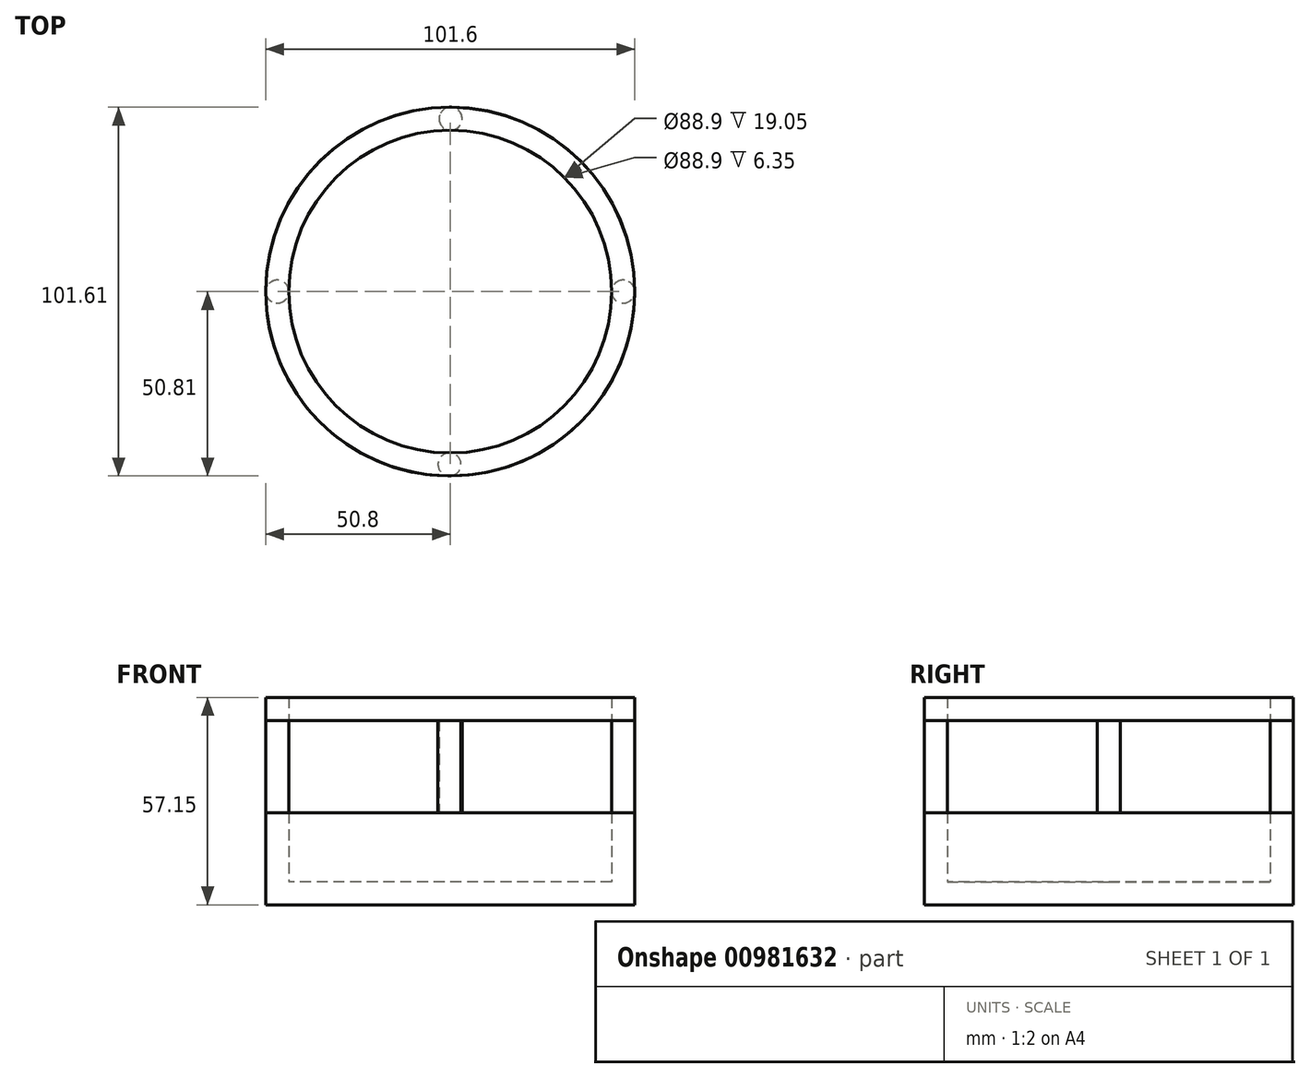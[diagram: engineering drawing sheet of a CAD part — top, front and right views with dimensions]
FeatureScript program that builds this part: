
annotation { "Feature Type Name" : "Feature", "Feature Type Description" : "" }
export const myFeature = defineFeature(function(context is Context, id is Id, definition is map)
    precondition{}
    {
        {
            var Q0;
            Q0=qCreatedBy(makeId("Top.planeOp"),FACE);
            var sketch = newSketch(context, id + "F0", { "sketchPlane" : qUnion([Q0])});
            skCircle(sketch, "E0", {"center": v(0, 0) * mm, "radius": 50.8 * mm});
            skCircle(sketch, "E1", {"center": v(0, 0) * mm, "radius": 44.45 * mm});
            skSolve(sketch);
        }
        {
            var Q0;
            Q0=makeQuery(id+"F0.imprint","IMPRINT",FACE,{"disambiguationData":[TD([[makeQuery(id+"F0.imprint","IMPRINT",EDGE,{"derivedFrom":sQuery(id+"F0.wireOp",EDGE,"E1")}),1.0]])]});
            extrude(context, id + "F1", {"entities" : qUnion([Q0]), "depth" : 6.35 * mm, "offsetDistance" : 25.4 * mm});
        }
        {
            var Q0;
            Q0=makeQuery(id+"F0.imprint","IMPRINT",FACE,{"disambiguationData":[TD([[makeQuery(id+"F0.imprint","IMPRINT",EDGE,{"derivedFrom":sQuery(id+"F0.wireOp",EDGE,"E0")}),1.0]])]});
            extrude(context, id + "F2", {"entities" : qUnion([Q0]), "operationType" : NewBodyOperationType.ADD, "depth" : 25.4 * mm, "offsetDistance" : 25.4 * mm});
        }
        {
            var Q0;
            Q0=makeQuery(id+"F2.opExtrude","CAP_FACE",FACE,{"disambiguationData":[OSD([sQuery(id+"F0.wireOp",EDGE,"E0"),sQuery(id+"F0.wireOp",EDGE,"E1")])],"isStart":false});
            var sketch = newSketch(context, id + "F3", { "sketchPlane" : qUnion([Q0])});
            skPoint(sketch, "E2", {"position": v(0, 48.03) * mm});
            skPoint(sketch, "E3", {"position": v(0, -47.72) * mm});
            skPoint(sketch, "E4", {"position": v(-48.02, 0) * mm});
            skPoint(sketch, "E5", {"position": v(47.66, 0) * mm});
            skCircle(sketch, "E6", {"center": v(-47.62, 0) * mm, "radius": 3.18 * mm});
            skPoint(sketch, "E6.first.point", {"position": v(-44.45, 0) * mm});
            skPoint(sketch, "E6.second.point", {"position": v(-50.8, 0) * mm});
            skPoint(sketch, "E6.third.point", {"position": v(-48.02, -3.15) * mm});
            skPoint(sketch, "E7", {"position": v(0, 50.8) * mm});
            skPoint(sketch, "E8", {"position": v(0, 44.45) * mm});
            skPoint(sketch, "E9", {"position": v(44.45, 0) * mm});
            skPoint(sketch, "E10", {"position": v(50.8, 0) * mm});
            skPoint(sketch, "E11", {"position": v(0, -44.45) * mm});
            skPoint(sketch, "E12", {"position": v(0, -50.8) * mm});
            skCircle(sketch, "E13", {"center": v(0.1, 47.62) * mm, "radius": 3.18 * mm});
            skPoint(sketch, "E13.first.point", {"position": v(0.28, 50.8) * mm});
            skPoint(sketch, "E13.third.point", {"position": v(-3.04, 48.03) * mm});
            skCircle(sketch, "E14", {"center": v(47.62, 0) * mm, "radius": 3.18 * mm});
            skPoint(sketch, "E14.third.point", {"position": v(47.66, 3.17) * mm});
            skCircle(sketch, "E15", {"center": v(-0.2, -47.63) * mm, "radius": 3.18 * mm});
            skPoint(sketch, "E15.first.point", {"position": v(-0.29, -44.46) * mm});
            skPoint(sketch, "E15.third.point", {"position": v(2.97, -47.72) * mm});
            skSolve(sketch);
        }
        {
            var Q0;
            {var subQ0=sQuery(id+"F3.wireOp",EDGE,"E14");var subQ1=makeQuery(id+"F3.imprint","INTERSECT",VERTEX,{"derivedFrom":[makeQuery(id+"F2.opExtrude","CAP_EDGE",EDGE,{"disambiguationData":[OSD([sQuery(id+"F0.wireOp",EDGE,"E0")])],"isStart":false}),subQ0]});Q0=makeQuery(id+"F3.imprint","IMPRINT",FACE,{"disambiguationData":[TD([[makeQuery(id+"F3.imprint","IMPRINT",EDGE,{"disambiguationData":[TD([[subQ1,-1.0]])],"derivedFrom":subQ0}),1.0]])]});}
            var Q1;
            {var subQ0=sQuery(id+"F3.wireOp",EDGE,"E15");var subQ1=makeQuery(id+"F2.opExtrude","CAP_EDGE",EDGE,{"disambiguationData":[OSD([sQuery(id+"F0.wireOp",EDGE,"E0")])],"isStart":false});var subQ2=makeQuery(id+"F3.imprint","INTERSECT",VERTEX,{"disambiguationData":[OD(0.0)],"derivedFrom":[subQ1,subQ0]});Q1=makeQuery(id+"F3.imprint","IMPRINT",FACE,{"disambiguationData":[TD([[makeQuery(id+"F3.imprint","IMPRINT",EDGE,{"disambiguationData":[TD([[subQ2,-1.0]])],"derivedFrom":subQ0}),1.0]])]});}
            var Q2;
            {var subQ0=sQuery(id+"F3.wireOp",EDGE,"E13");var subQ1=makeQuery(id+"F2.opExtrude","CAP_EDGE",EDGE,{"disambiguationData":[OSD([sQuery(id+"F0.wireOp",EDGE,"E1")])],"isStart":false});var subQ2=makeQuery(id+"F3.imprint","INTERSECT",VERTEX,{"disambiguationData":[OD(0.0)],"derivedFrom":[subQ1,subQ0]});Q2=makeQuery(id+"F3.imprint","IMPRINT",FACE,{"disambiguationData":[TD([[makeQuery(id+"F3.imprint","IMPRINT",EDGE,{"disambiguationData":[TD([[subQ2,-1.0]])],"derivedFrom":subQ0}),1.0]])]});}
            var Q3;
            {var subQ0=sQuery(id+"F3.wireOp",EDGE,"E13");var subQ1=makeQuery(id+"F2.opExtrude","CAP_EDGE",EDGE,{"disambiguationData":[OSD([sQuery(id+"F0.wireOp",EDGE,"E1")])],"isStart":false});var subQ2=makeQuery(id+"F3.imprint","INTERSECT",VERTEX,{"disambiguationData":[OD(0.0)],"derivedFrom":[subQ1,subQ0]});Q3=makeQuery(id+"F3.imprint","IMPRINT",FACE,{"disambiguationData":[TD([[makeQuery(id+"F3.imprint","IMPRINT",EDGE,{"disambiguationData":[TD([[subQ2,1.0]])],"derivedFrom":subQ0}),1.0]])]});}
            var Q4;
            {var subQ0=sQuery(id+"F3.wireOp",EDGE,"E15");var subQ1=makeQuery(id+"F2.opExtrude","CAP_EDGE",EDGE,{"disambiguationData":[OSD([sQuery(id+"F0.wireOp",EDGE,"E0")])],"isStart":false});var subQ2=makeQuery(id+"F3.imprint","INTERSECT",VERTEX,{"disambiguationData":[OD(0.0)],"derivedFrom":[subQ1,subQ0]});Q4=makeQuery(id+"F3.imprint","IMPRINT",FACE,{"disambiguationData":[TD([[makeQuery(id+"F3.imprint","IMPRINT",EDGE,{"disambiguationData":[TD([[subQ2,1.0]])],"derivedFrom":subQ0}),1.0]])]});}
            var Q5;
            {var subQ0=sQuery(id+"F3.wireOp",EDGE,"E6");var subQ1=makeQuery(id+"F3.imprint","INTERSECT",VERTEX,{"derivedFrom":[makeQuery(id+"F2.opExtrude","CAP_EDGE",EDGE,{"disambiguationData":[OSD([sQuery(id+"F0.wireOp",EDGE,"E0")])],"isStart":false}),subQ0]});Q5=makeQuery(id+"F3.imprint","IMPRINT",FACE,{"disambiguationData":[TD([[makeQuery(id+"F3.imprint","IMPRINT",EDGE,{"disambiguationData":[TD([[subQ1,1.0]])],"derivedFrom":subQ0}),1.0]])]});}
            extrude(context, id + "F4", {"entities" : qUnion([Q0, Q1, Q2, Q3, Q4, Q5]), "operationType" : NewBodyOperationType.ADD, "depth" : 25.4 * mm, "offsetDistance" : 25.4 * mm});
        }
        {
            var Q0;
            Q0=makeQuery(id+"F4.opExtrude","CAP_FACE",FACE,{"disambiguationData":[OSD([sQuery(id+"F3.wireOp",EDGE,"E15")])],"isStart":false});
            var sketch = newSketch(context, id + "F5", { "sketchPlane" : qUnion([Q0])});
            skCircle(sketch, "E16", {"center": v(0, 0) * mm, "radius": 50.78 * mm});
            skCircle(sketch, "E17", {"center": v(0, 0) * mm, "radius": 44.45 * mm});
            skSolve(sketch);
        }
        {
            var Q0;
            Q0=makeQuery(id+"F5.imprint","IMPRINT",FACE,{"disambiguationData":[TD([[makeQuery(id+"F5.imprint","IMPRINT",EDGE,{"derivedFrom":sQuery(id+"F5.wireOp",EDGE,"E17")}),-1.0]])]});
            var Q1;
            {var subQ0=sQuery(id+"F5.wireOp",EDGE,"E16");var subQ1=makeQuery(id+"F4.opExtrude","CAP_EDGE",EDGE,{"disambiguationData":[OSD([sQuery(id+"F3.wireOp",EDGE,"E15")])],"isStart":false});var subQ2=makeQuery(id+"F5.imprint","INTERSECT",VERTEX,{"disambiguationData":[OD(0.0)],"derivedFrom":[subQ1,subQ0]});Q1=makeQuery(id+"F5.imprint","IMPRINT",FACE,{"disambiguationData":[TD([[makeQuery(id+"F5.imprint","IMPRINT",EDGE,{"disambiguationData":[TD([[subQ2,-1.0]])],"derivedFrom":subQ0}),1.0]])]});}
            extrude(context, id + "F6", {"entities" : qUnion([Q0, Q1]), "operationType" : NewBodyOperationType.ADD, "depth" : 6.35 * mm, "offsetDistance" : 25.4 * mm});
        }
    });
